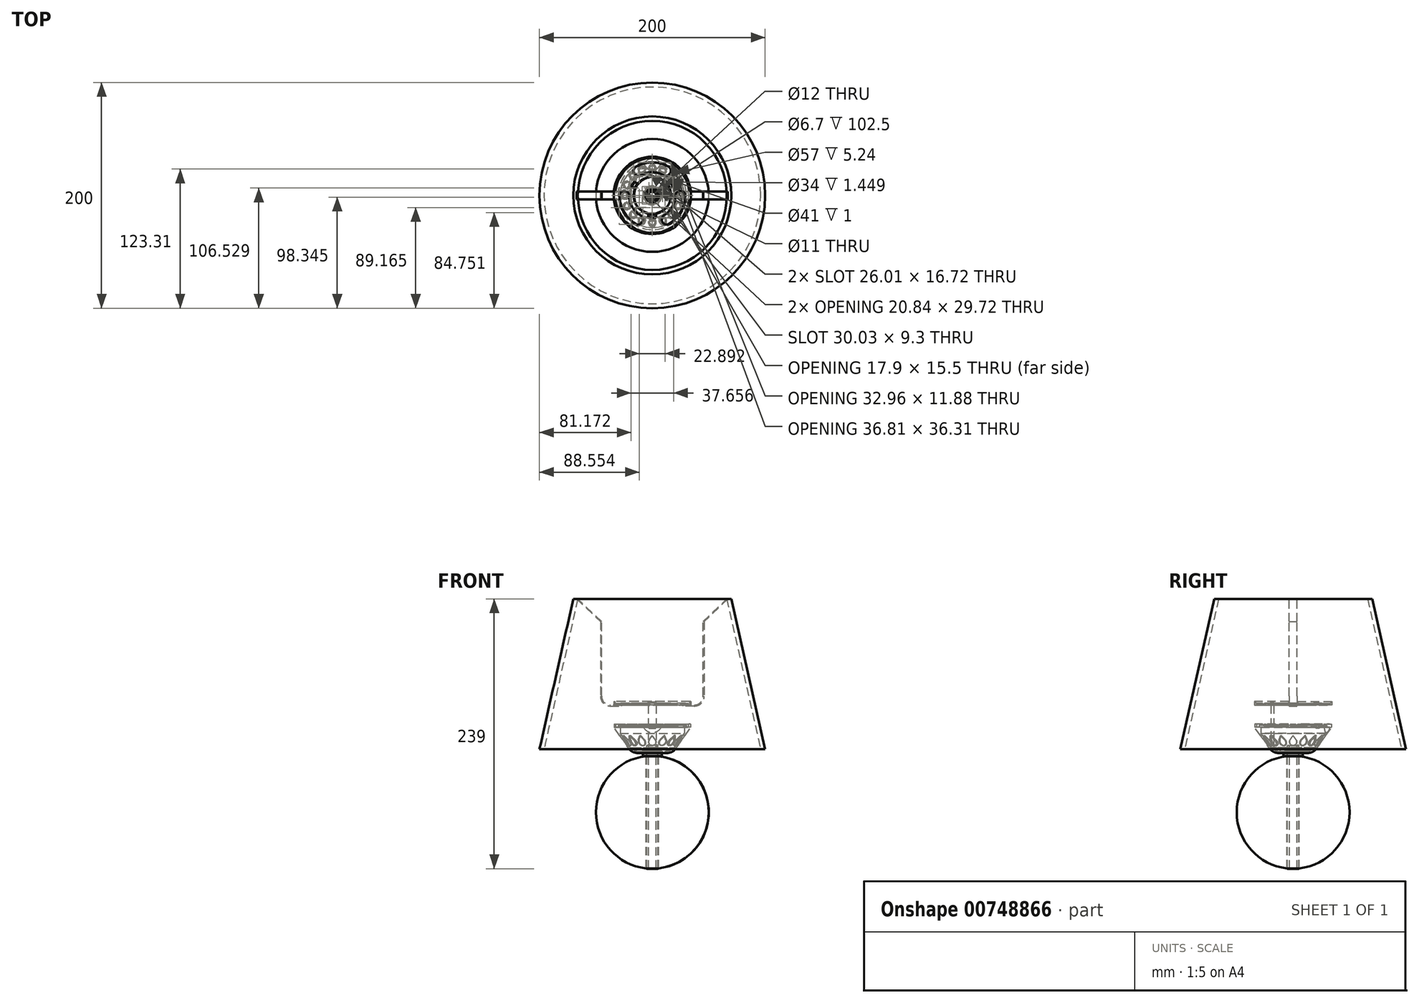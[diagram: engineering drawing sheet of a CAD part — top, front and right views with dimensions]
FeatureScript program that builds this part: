
annotation { "Feature Type Name" : "Feature", "Feature Type Description" : "" }
export const myFeature = defineFeature(function(context is Context, id is Id, definition is map)
    precondition{}
    {
        {
            assignVariable(context, id + "F0", {"name" : "e", "anyValue" : 1.5});
        }
        {
            var Q0;
            Q0=qCreatedBy(makeId("Front.planeOp"),FACE);
            var sketch = newSketch(context, id + "F1", { "sketchPlane" : qUnion([Q0])});
            skLineSegment(sketch, "E0", {"start": v(0, 0) * mm, "end": v(0, -12.75) * mm, "construction": true});
            skLineSegment(sketch, "E1.bottom", {"start": v(-3.35, 5) * mm, "end": v(-5, 5) * mm});
            skLineSegment(sketch, "E1.top", {"start": v(-3.35, -105) * mm, "end": v(-5, -105) * mm});
            skLineSegment(sketch, "E1.left", {"start": v(-3.35, 5) * mm, "end": v(-3.35, -105) * mm});
            skLineSegment(sketch, "E1.right", {"start": v(-5, 5) * mm, "end": v(-5, -105) * mm});
            skSolve(sketch);
        }
        {
            var Q0;
            Q0=makeQuery(id+"F1.imprint","IMPRINT",FACE,{"disambiguationData":[TD([[makeQuery(id+"F1.imprint","IMPRINT",EDGE,{"derivedFrom":sQuery(id+"F1.wireOp",EDGE,"E1.bottom")}),1.0]])]});
            var Q1;
            Q1=sQuery(id+"F1.wireOp",EDGE,"E0");
            revolve(context, id + "F2", {"surfaceOperationType" : NewSurfaceOperationType.NEW, "entities" : qUnion([Q0]), "axis" : qUnion([Q1]), "revolveType" : RevolveType.FULL});
        }
        {
            var Q0;
            Q0=qCreatedBy(makeId("Top.planeOp"),FACE);
            var sketch = newSketch(context, id + "F3", { "sketchPlane" : qUnion([Q0])});
            skLineSegment(sketch, "E2", {"start": v(0, 7) * mm, "end": v(-4.04, 7) * mm});
            skLineSegment(sketch, "E3", {"start": v(-4.04, 7) * mm, "end": v(-8.08, 0) * mm});
            skLineSegment(sketch, "E4", {"start": v(-8.08, 0) * mm, "end": v(0, 0) * mm, "construction": true});
            skLineSegment(sketch, "E5", {"start": v(0, 0) * mm, "end": v(0, 7) * mm, "construction": true});
            skLineSegment(sketch, "E6.MirrorCS", {"start": v(4.04, 7) * mm, "end": v(8.08, 0) * mm});
            skLineSegment(sketch, "E7.MirrorCS", {"start": v(0, 7) * mm, "end": v(4.04, 7) * mm});
            skLineSegment(sketch, "E8.MirrorCS", {"start": v(-4.04, -7) * mm, "end": v(-8.08, 0) * mm});
            skLineSegment(sketch, "E9.MirrorCS", {"start": v(0, -7) * mm, "end": v(-4.04, -7) * mm});
            skLineSegment(sketch, "E10.MirrorCS", {"start": v(0, -7) * mm, "end": v(4.04, -7) * mm});
            skLineSegment(sketch, "E11.MirrorCS", {"start": v(4.04, -7) * mm, "end": v(8.08, 0) * mm});
            skCircle(sketch, "E12", {"center": v(0, 0) * mm, "radius": 5 * mm});
            skSolve(sketch);
        }
        {
            var Q0;
            Q0=makeQuery(id+"F3.imprint","IMPRINT",FACE,{"disambiguationData":[TD([[makeQuery(id+"F3.imprint","IMPRINT",EDGE,{"derivedFrom":sQuery(id+"F3.wireOp",EDGE,"E2")}),1.0]])]});
            extrude(context, id + "F4", {"entities" : qUnion([Q0]), "oppositeDirection" : true, "depth" : 2.5 * mm, "offsetDistance" : 25 * mm});
        }
        {
            var Q0;
            Q0=makeQuery(id+"F4.opExtrude","CAP_FACE",FACE,{"disambiguationData":[OSD([sQuery(id+"F3.wireOp",EDGE,"E2"),sQuery(id+"F3.wireOp",EDGE,"E3"),sQuery(id+"F3.wireOp",EDGE,"E6.MirrorCS"),sQuery(id+"F3.wireOp",EDGE,"E7.MirrorCS"),sQuery(id+"F3.wireOp",EDGE,"E8.MirrorCS"),sQuery(id+"F3.wireOp",EDGE,"E9.MirrorCS"),sQuery(id+"F3.wireOp",EDGE,"E10.MirrorCS"),sQuery(id+"F3.wireOp",EDGE,"E11.MirrorCS"),sQuery(id+"F3.wireOp",EDGE,"E12")])],"isStart":false});
            var sketch = newSketch(context, id + "F5", { "sketchPlane" : qUnion([Q0])});
            skCircle(sketch, "E13", {"center": v(0, 0) * mm, "radius": 5 * mm});
            skCircle(sketch, "E14", {"center": v(0, 0) * mm, "radius": 8.5 * mm});
            skSolve(sketch);
        }
        {
            var Q0;
            Q0=makeQuery(id+"F5.imprint","IMPRINT",FACE,{"disambiguationData":[TD([[makeQuery(id+"F5.imprint","IMPRINT",EDGE,{"derivedFrom":sQuery(id+"F5.wireOp",EDGE,"E14")}),1.0]])]});
            var Q1;
            Q1=makeQuery(id+"F5.imprint","IMPRINT",FACE,{"disambiguationData":[TD([[makeQuery(id+"F5.imprint","IMPRINT",EDGE,{"derivedFrom":sQuery(id+"F5.wireOp",EDGE,"E13")}),1.0]])]});
            extrude(context, id + "F6", {"entities" : qUnion([Q0, Q1]), "depth" : 2.5 * mm, "offsetDistance" : 25 * mm});
        }
        {
            var Q0;
            Q0=qCreatedBy(makeId("Front.planeOp"),FACE);
            var sketch = newSketch(context, id + "F7", { "sketchPlane" : qUnion([Q0])});
            skArc(sketch, "E15", {"start": v(0, -5) * mm, "mid": v(-50, -55) * mm, "end": v(0, -105) * mm});
            skLineSegment(sketch, "E16.0", {"start": v(8.5, -5) * mm, "end": v(-8.5, -5) * mm});
            skLineSegment(sketch, "E17", {"start": v(0, -5) * mm, "end": v(0, -105) * mm});
            skSolve(sketch);
        }
        {
            var Q0;
            Q0=makeQuery(id+"F7.imprint","IMPRINT",FACE,{"disambiguationData":[TD([[makeQuery(id+"F7.imprint","IMPRINT",EDGE,{"derivedFrom":sQuery(id+"F7.wireOp",EDGE,"E15")}),1.0]])]});
            var Q1;
            Q1=sQuery(id+"F7.wireOp",EDGE,"E17");
            revolve(context, id + "F8", {"surfaceOperationType" : NewSurfaceOperationType.NEW, "entities" : qUnion([Q0]), "axis" : qUnion([Q1]), "revolveType" : RevolveType.FULL});
        }
        {
            var Q0;
            Q0=sQuery(id+"F3.wireOp",VERTEX,"E12.center");
            var Q1;
            Q1=makeQuery(id+"F8.opRevolve","SWEPT_BODY",BODY,{"disambiguationData":[OSD([sQuery(id+"F7.wireOp",EDGE,"E15"),sQuery(id+"F7.wireOp",EDGE,"E17")])]});
            hole(context, id + "F9", {"style" : HoleStyle.SIMPLE, "endStyle" : HoleEndStyle.THROUGH, "holeDiameter" : 11 * mm, "majorDiameter" : 5 * mm, "isTappedThrough" : true, "tappedDepth" : 12 * mm, "tapClearance" : 3, "locations" : qUnion([Q0]), "scope" : qUnion([Q1])});
        }
        {
            var Q0;
            Q0=qCreatedBy(makeId("Front.planeOp"),FACE);
            var sketch = newSketch(context, id + "F10", { "sketchPlane" : qUnion([Q0])});
            skLineSegment(sketch, "E18", {"start": v(0, -13.04) * mm, "end": v(0, 48.26) * mm, "construction": true});
            skLineSegment(sketch, "E19", {"start": v(-21.07, 1.76) * mm, "end": v(-34, 20.23) * mm});
            skLineSegment(sketch, "E20", {"start": v(-34, 20.23) * mm, "end": v(-34, 23.23) * mm});
            skLineSegment(sketch, "E21", {"start": v(-34, 23.23) * mm, "end": v(-32.5, 23.23) * mm});
            skLineSegment(sketch, "E22", {"start": v(-32.5, 23.23) * mm, "end": v(-32.5, 20.23) * mm});
            skLineSegment(sketch, "E23", {"start": v(-28.5, 15) * mm, "end": v(-19.5, 2.14) * mm});
            skLineSegment(sketch, "E24", {"start": v(-12.08, -1) * mm, "end": v(0, -1) * mm});
            skLineSegment(sketch, "E25", {"start": v(0, -1) * mm, "end": v(0, -2.5) * mm});
            skLineSegment(sketch, "E26.0", {"start": v(-8.08, -2.5) * mm, "end": v(-8.08, 0) * mm, "construction": true});
            skLineSegment(sketch, "E27.0", {"start": v(8.5, -2.5) * mm, "end": v(-8.5, -2.5) * mm});
            skLineSegment(sketch, "E28", {"start": v(-12.88, -2.5) * mm, "end": v(0, -2.5) * mm});
            skLineSegment(sketch, "E29", {"start": v(-28.5, 15) * mm, "end": v(-28.5, 20.23) * mm});
            skLineSegment(sketch, "E30", {"start": v(-28.5, 20.23) * mm, "end": v(-32.5, 20.23) * mm});
            skLineSegment(sketch, "E31", {"start": v(-17, 0.7) * mm, "end": v(-17, 2.14) * mm});
            skLineSegment(sketch, "E32", {"start": v(-17, 2.14) * mm, "end": v(-19.5, 2.14) * mm});
            skPoint(sketch, "E33.visualSharp", {"position": v(-18.08, -2.5) * mm});
            skArc(sketch, "E33.filletArc", {"start": v(-21.07, 1.76) * mm, "mid": v(-17.5, -1.37) * mm, "end": v(-12.88, -2.5) * mm});
            skPoint(sketch, "E34.visualSharp", {"position": v(-14.3, -1) * mm});
            skArc(sketch, "E34.filletArc", {"start": v(-17, 0.7) * mm, "mid": v(-14.68, -0.57) * mm, "end": v(-12.08, -1) * mm});
            skSolve(sketch);
        }
        {
            var Q0;
            {var subQ1=sQuery(id+"F10.wireOp",EDGE,"E19");Q0=makeQuery(id+"F10.imprint","IMPRINT",FACE,{"disambiguationData":[TD([[makeQuery(id+"F10.imprint","IMPRINT",EDGE,{"derivedFrom":subQ1}),-1.0]])]});}
            var Q1;
            Q1=sQuery(id+"F10.wireOp",EDGE,"E18");
            revolve(context, id + "F11", {"surfaceOperationType" : NewSurfaceOperationType.NEW, "entities" : qUnion([Q0]), "axis" : qUnion([Q1]), "revolveType" : RevolveType.FULL});
        }
        {
            var Q0;
            Q0=makeQuery(id+"F11.opRevolve","SWEPT_FACE",FACE,{"disambiguationData":[OSD([sQuery(id+"F10.wireOp",EDGE,"E24")])]});
            var sketch = newSketch(context, id + "F12", { "sketchPlane" : qUnion([Q0])});
            skLineSegment(sketch, "E35", {"start": v(-4.04, -7) * mm, "end": v(-8.08, 0) * mm, "construction": true});
            skLineSegment(sketch, "E36", {"start": v(4.04, -7) * mm, "end": v(-4.04, -7) * mm, "construction": true});
            skLineSegment(sketch, "E37", {"start": v(4.04, -7) * mm, "end": v(8.08, 0) * mm, "construction": true});
            skLineSegment(sketch, "E38", {"start": v(4.04, 7) * mm, "end": v(8.08, 0) * mm, "construction": true});
            skLineSegment(sketch, "E39", {"start": v(-4.04, 7) * mm, "end": v(4.04, 7) * mm, "construction": true});
            skLineSegment(sketch, "E40", {"start": v(-4.04, 7) * mm, "end": v(-8.08, 0) * mm, "construction": true});
            skLineSegment(sketch, "E41.0", {"start": v(-4.47, 7.75) * mm, "end": v(4.47, 7.75) * mm});
            skLineSegment(sketch, "E41.1", {"start": v(-4.47, -7.75) * mm, "end": v(-8.95, 0) * mm});
            skLineSegment(sketch, "E41.2", {"start": v(4.47, -7.75) * mm, "end": v(-4.47, -7.75) * mm});
            skLineSegment(sketch, "E41.3", {"start": v(-4.47, 7.75) * mm, "end": v(-8.95, 0) * mm});
            skLineSegment(sketch, "E41.4", {"start": v(4.47, -7.75) * mm, "end": v(8.95, 0) * mm});
            skLineSegment(sketch, "E41.5", {"start": v(4.47, 7.75) * mm, "end": v(8.95, 0) * mm});
            skSolve(sketch);
        }
        {
            var Q0;
            Q0=makeQuery(id+"F12.imprint","IMPRINT",FACE,{"disambiguationData":[TD([[makeQuery(id+"F12.imprint","IMPRINT",EDGE,{"derivedFrom":sQuery(id+"F12.wireOp",EDGE,"E41.0")}),-1.0]])]});
            extrude(context, id + "F13", {"entities" : qUnion([Q0]), "operationType" : NewBodyOperationType.REMOVE, "endBound" : BoundingType.UP_TO_NEXT, "oppositeDirection" : true, "depth" : 25 * mm, "offsetDistance" : 25 * mm});
        }
        {
            var Q0;
            Q0=makeQuery(id+"F11.opRevolve","SWEPT_FACE",FACE,{"disambiguationData":[OSD([sQuery(id+"F10.wireOp",EDGE,"E30")])]});
            var sketch = newSketch(context, id + "F14", { "sketchPlane" : qUnion([Q0])});
            skCircle(sketch, "E42", {"center": v(0, 0) * mm, "radius": 30.3 * mm});
            skLineSegment(sketch, "E43", {"start": v(0, 0) * mm, "end": v(-3.08, 15.85) * mm, "construction": true});
            skLineSegment(sketch, "E44.MirrorCS", {"start": v(0, 0) * mm, "end": v(3.08, 15.85) * mm, "construction": true});
            skLineSegment(sketch, "E45.1.0", {"start": v(0, 0) * mm, "end": v(-12.19, -10.6) * mm, "construction": true});
            skLineSegment(sketch, "E45.1.1", {"start": v(0, 0) * mm, "end": v(-15.27, -5.26) * mm, "construction": true});
            skLineSegment(sketch, "E45.2.0", {"start": v(0, 0) * mm, "end": v(15.27, -5.26) * mm, "construction": true});
            skLineSegment(sketch, "E45.2.1", {"start": v(0, 0) * mm, "end": v(12.19, -10.6) * mm, "construction": true});
            skLineSegment(sketch, "E46", {"start": v(-3.08, 15.85) * mm, "end": v(-3.8, 19.53) * mm});
            skLineSegment(sketch, "E47", {"start": v(3.08, 15.85) * mm, "end": v(3.8, 19.53) * mm});
            skArc(sketch, "E48", {"start": v(3.8, 19.53) * mm, "mid": v(0, 19.9) * mm, "end": v(-3.8, 19.53) * mm, "construction": true});
            skArc(sketch, "E49", {"start": v(-3.8, 19.53) * mm, "mid": v(-17.23, 9.95) * mm, "end": v(-18.82, -6.48) * mm});
            skArc(sketch, "E50", {"start": v(-3.08, 15.85) * mm, "mid": v(-13.99, 8.07) * mm, "end": v(-15.27, -5.26) * mm});
            skArc(sketch, "E51", {"start": v(3.08, 15.85) * mm, "mid": v(0, 16.15) * mm, "end": v(-3.08, 15.85) * mm, "construction": true});
            skArc(sketch, "E52", {"start": v(15.27, -5.26) * mm, "mid": v(13.99, 8.07) * mm, "end": v(3.08, 15.85) * mm});
            skLineSegment(sketch, "E53", {"start": v(15.27, -5.26) * mm, "end": v(18.82, -6.48) * mm});
            skArc(sketch, "E54", {"start": v(18.82, -6.48) * mm, "mid": v(17.23, 9.95) * mm, "end": v(3.8, 19.53) * mm});
            skArc(sketch, "E55", {"start": v(15.02, -13.06) * mm, "mid": v(17.23, -9.95) * mm, "end": v(18.82, -6.48) * mm, "construction": true});
            skLineSegment(sketch, "E56", {"start": v(12.19, -10.6) * mm, "end": v(15.02, -13.06) * mm});
            skArc(sketch, "E57", {"start": v(12.19, -10.6) * mm, "mid": v(13.99, -8.08) * mm, "end": v(15.27, -5.26) * mm, "construction": true});
            skArc(sketch, "E58", {"start": v(-12.19, -10.6) * mm, "mid": v(0, -16.15) * mm, "end": v(12.19, -10.6) * mm});
            skLineSegment(sketch, "E59", {"start": v(-12.19, -10.6) * mm, "end": v(-15.02, -13.06) * mm});
            skArc(sketch, "E60", {"start": v(-15.27, -5.26) * mm, "mid": v(-13.99, -8.07) * mm, "end": v(-12.19, -10.6) * mm, "construction": true});
            skLineSegment(sketch, "E61", {"start": v(-15.27, -5.26) * mm, "end": v(-18.82, -6.48) * mm});
            skArc(sketch, "E62", {"start": v(-18.82, -6.48) * mm, "mid": v(-17.23, -9.95) * mm, "end": v(-15.02, -13.06) * mm, "construction": true});
            skArc(sketch, "E63", {"start": v(-15.02, -13.06) * mm, "mid": v(0, -19.9) * mm, "end": v(15.02, -13.06) * mm});
            skSolve(sketch);
        }
        {
            var Q0;
            Q0=makeQuery(id+"F14.imprint","IMPRINT",FACE,{"disambiguationData":[TD([[makeQuery(id+"F14.imprint","IMPRINT",EDGE,{"derivedFrom":sQuery(id+"F14.wireOp",EDGE,"E46")}),-1.0]])]});
            var Q1;
            Q1=makeQuery(id+"F14.imprint","IMPRINT",FACE,{"disambiguationData":[TD([[makeQuery(id+"F14.imprint","IMPRINT",EDGE,{"derivedFrom":sQuery(id+"F14.wireOp",EDGE,"E42")}),1.0]])]});
            extrude(context, id + "F15", {"entities" : qUnion([Q0, Q1]), "depth" : 1.5 * mm, "offsetDistance" : 25 * mm});
        }
        {
            var Q0;
            Q0=makeQuery(id+"F15.opExtrude","CAP_FACE",FACE,{"disambiguationData":[OSD([sQuery(id+"F10.wireOp",EDGE,"E29"),sQuery(id+"F10.wireOp",EDGE,"E30"),sQuery(id+"F14.wireOp",EDGE,"E46"),sQuery(id+"F14.wireOp",EDGE,"E47"),sQuery(id+"F14.wireOp",EDGE,"E49"),sQuery(id+"F14.wireOp",EDGE,"E50"),sQuery(id+"F14.wireOp",EDGE,"E52"),sQuery(id+"F14.wireOp",EDGE,"E53"),sQuery(id+"F14.wireOp",EDGE,"E54"),sQuery(id+"F14.wireOp",EDGE,"E56"),sQuery(id+"F14.wireOp",EDGE,"E58"),sQuery(id+"F14.wireOp",EDGE,"E59"),sQuery(id+"F14.wireOp",EDGE,"E61"),sQuery(id+"F14.wireOp",EDGE,"E63")])],"isStart":false});
            var sketch = newSketch(context, id + "F16", { "sketchPlane" : qUnion([Q0])});
            skLineSegment(sketch, "E64.bottom", {"start": v(2.5, 26.95) * mm, "end": v(-2.5, 26.95) * mm});
            skLineSegment(sketch, "E64.top", {"start": v(2.5, 21.95) * mm, "end": v(-2.5, 21.95) * mm});
            skLineSegment(sketch, "E64.left", {"start": v(2.5, 26.95) * mm, "end": v(2.5, 21.95) * mm});
            skLineSegment(sketch, "E64.right", {"start": v(-2.5, 26.95) * mm, "end": v(-2.5, 21.95) * mm});
            skPoint(sketch, "E64.middle", {"position": v(0, 24.45) * mm});
            skLineSegment(sketch, "E65.1.0", {"start": v(-8, 25.86) * mm, "end": v(-12.62, 23.94) * mm});
            skLineSegment(sketch, "E65.1.1", {"start": v(-12.62, 23.94) * mm, "end": v(-10.7, 19.32) * mm});
            skLineSegment(sketch, "E65.1.2", {"start": v(-6.1, 21.24) * mm, "end": v(-10.7, 19.32) * mm});
            skLineSegment(sketch, "E65.1.3", {"start": v(-8, 25.86) * mm, "end": v(-6.1, 21.24) * mm});
            skLineSegment(sketch, "E65.2.0", {"start": v(-17.29, 20.82) * mm, "end": v(-20.82, 17.29) * mm});
            skLineSegment(sketch, "E65.2.1", {"start": v(-20.82, 17.29) * mm, "end": v(-17.29, 13.75) * mm});
            skLineSegment(sketch, "E65.2.2", {"start": v(-13.75, 17.29) * mm, "end": v(-17.29, 13.75) * mm});
            skLineSegment(sketch, "E65.2.3", {"start": v(-17.29, 20.82) * mm, "end": v(-13.75, 17.29) * mm});
            skLineSegment(sketch, "E65.3.0", {"start": v(-23.94, 12.62) * mm, "end": v(-25.86, 8) * mm});
            skLineSegment(sketch, "E65.3.1", {"start": v(-25.86, 8) * mm, "end": v(-21.24, 6.1) * mm});
            skLineSegment(sketch, "E65.3.2", {"start": v(-19.32, 10.7) * mm, "end": v(-21.24, 6.1) * mm});
            skLineSegment(sketch, "E65.3.3", {"start": v(-23.94, 12.62) * mm, "end": v(-19.32, 10.7) * mm});
            skLineSegment(sketch, "E65.4.0", {"start": v(-26.95, 2.5) * mm, "end": v(-26.95, -2.5) * mm});
            skLineSegment(sketch, "E65.4.1", {"start": v(-26.95, -2.5) * mm, "end": v(-21.95, -2.5) * mm});
            skLineSegment(sketch, "E65.4.2", {"start": v(-21.95, 2.5) * mm, "end": v(-21.95, -2.5) * mm});
            skLineSegment(sketch, "E65.4.3", {"start": v(-26.95, 2.5) * mm, "end": v(-21.95, 2.5) * mm});
            skLineSegment(sketch, "E65.5.0", {"start": v(-25.86, -8) * mm, "end": v(-23.94, -12.62) * mm});
            skLineSegment(sketch, "E65.5.1", {"start": v(-23.94, -12.62) * mm, "end": v(-19.32, -10.7) * mm});
            skLineSegment(sketch, "E65.5.2", {"start": v(-21.24, -6.1) * mm, "end": v(-19.32, -10.7) * mm});
            skLineSegment(sketch, "E65.5.3", {"start": v(-25.86, -8) * mm, "end": v(-21.24, -6.1) * mm});
            skLineSegment(sketch, "E65.6.0", {"start": v(-20.82, -17.29) * mm, "end": v(-17.29, -20.82) * mm});
            skLineSegment(sketch, "E65.6.1", {"start": v(-17.29, -20.82) * mm, "end": v(-13.75, -17.29) * mm});
            skLineSegment(sketch, "E65.6.2", {"start": v(-17.29, -13.75) * mm, "end": v(-13.75, -17.29) * mm});
            skLineSegment(sketch, "E65.6.3", {"start": v(-20.82, -17.29) * mm, "end": v(-17.29, -13.75) * mm});
            skLineSegment(sketch, "E65.7.0", {"start": v(-12.62, -23.94) * mm, "end": v(-8, -25.86) * mm});
            skLineSegment(sketch, "E65.7.1", {"start": v(-8, -25.86) * mm, "end": v(-6.1, -21.24) * mm});
            skLineSegment(sketch, "E65.7.2", {"start": v(-10.7, -19.32) * mm, "end": v(-6.1, -21.24) * mm});
            skLineSegment(sketch, "E65.7.3", {"start": v(-12.62, -23.94) * mm, "end": v(-10.7, -19.32) * mm});
            skLineSegment(sketch, "E65.8.0", {"start": v(-2.5, -26.95) * mm, "end": v(2.5, -26.95) * mm});
            skLineSegment(sketch, "E65.8.1", {"start": v(2.5, -26.95) * mm, "end": v(2.5, -21.95) * mm});
            skLineSegment(sketch, "E65.8.2", {"start": v(-2.5, -21.95) * mm, "end": v(2.5, -21.95) * mm});
            skLineSegment(sketch, "E65.8.3", {"start": v(-2.5, -26.95) * mm, "end": v(-2.5, -21.95) * mm});
            skLineSegment(sketch, "E65.9.0", {"start": v(8, -25.86) * mm, "end": v(12.62, -23.94) * mm});
            skLineSegment(sketch, "E65.9.1", {"start": v(12.62, -23.94) * mm, "end": v(10.7, -19.32) * mm});
            skLineSegment(sketch, "E65.9.2", {"start": v(6.1, -21.24) * mm, "end": v(10.7, -19.32) * mm});
            skLineSegment(sketch, "E65.9.3", {"start": v(8, -25.86) * mm, "end": v(6.1, -21.24) * mm});
            skLineSegment(sketch, "E65.10.0", {"start": v(17.29, -20.82) * mm, "end": v(20.82, -17.29) * mm});
            skLineSegment(sketch, "E65.10.1", {"start": v(20.82, -17.29) * mm, "end": v(17.29, -13.75) * mm});
            skLineSegment(sketch, "E65.10.2", {"start": v(13.75, -17.29) * mm, "end": v(17.29, -13.75) * mm});
            skLineSegment(sketch, "E65.10.3", {"start": v(17.29, -20.82) * mm, "end": v(13.75, -17.29) * mm});
            skLineSegment(sketch, "E65.11.0", {"start": v(23.94, -12.62) * mm, "end": v(25.86, -8) * mm});
            skLineSegment(sketch, "E65.11.1", {"start": v(25.86, -8) * mm, "end": v(21.24, -6.1) * mm});
            skLineSegment(sketch, "E65.11.2", {"start": v(19.32, -10.7) * mm, "end": v(21.24, -6.1) * mm});
            skLineSegment(sketch, "E65.11.3", {"start": v(23.94, -12.62) * mm, "end": v(19.32, -10.7) * mm});
            skLineSegment(sketch, "E65.12.0", {"start": v(26.95, -2.5) * mm, "end": v(26.95, 2.5) * mm});
            skLineSegment(sketch, "E65.12.1", {"start": v(26.95, 2.5) * mm, "end": v(21.95, 2.5) * mm});
            skLineSegment(sketch, "E65.12.2", {"start": v(21.95, -2.5) * mm, "end": v(21.95, 2.5) * mm});
            skLineSegment(sketch, "E65.12.3", {"start": v(26.95, -2.5) * mm, "end": v(21.95, -2.5) * mm});
            skLineSegment(sketch, "E65.13.0", {"start": v(25.86, 8) * mm, "end": v(23.94, 12.62) * mm});
            skLineSegment(sketch, "E65.13.1", {"start": v(23.94, 12.62) * mm, "end": v(19.32, 10.7) * mm});
            skLineSegment(sketch, "E65.13.2", {"start": v(21.24, 6.1) * mm, "end": v(19.32, 10.7) * mm});
            skLineSegment(sketch, "E65.13.3", {"start": v(25.86, 8) * mm, "end": v(21.24, 6.1) * mm});
            skLineSegment(sketch, "E65.14.0", {"start": v(20.82, 17.29) * mm, "end": v(17.29, 20.82) * mm});
            skLineSegment(sketch, "E65.14.1", {"start": v(17.29, 20.82) * mm, "end": v(13.75, 17.29) * mm});
            skLineSegment(sketch, "E65.14.2", {"start": v(17.29, 13.75) * mm, "end": v(13.75, 17.29) * mm});
            skLineSegment(sketch, "E65.14.3", {"start": v(20.82, 17.29) * mm, "end": v(17.29, 13.75) * mm});
            skLineSegment(sketch, "E65.15.0", {"start": v(12.62, 23.94) * mm, "end": v(8, 25.86) * mm});
            skLineSegment(sketch, "E65.15.1", {"start": v(8, 25.86) * mm, "end": v(6.1, 21.24) * mm});
            skLineSegment(sketch, "E65.15.2", {"start": v(10.7, 19.32) * mm, "end": v(6.1, 21.24) * mm});
            skLineSegment(sketch, "E65.15.3", {"start": v(12.62, 23.94) * mm, "end": v(10.7, 19.32) * mm});
            skPoint(sketch, "E65.center", {"position": v(0, 0) * mm});
            skSolve(sketch);
        }
        {
            var Q0;
            Q0 = qSketchRegion(id + "F16", true);
            extrude(context, id + "F17", {"entities" : qUnion([Q0]), "operationType" : NewBodyOperationType.ADD, "depth" : 1 * mm, "offsetDistance" : 25 * mm});
        }
        {
            var Q0;
            Q0=makeQuery(id+"F15.opExtrude","CAP_FACE",FACE,{"disambiguationData":[OSD([sQuery(id+"F10.wireOp",EDGE,"E29"),sQuery(id+"F10.wireOp",EDGE,"E30"),sQuery(id+"F14.wireOp",EDGE,"E46"),sQuery(id+"F14.wireOp",EDGE,"E47"),sQuery(id+"F14.wireOp",EDGE,"E49"),sQuery(id+"F14.wireOp",EDGE,"E50"),sQuery(id+"F14.wireOp",EDGE,"E52"),sQuery(id+"F14.wireOp",EDGE,"E53"),sQuery(id+"F14.wireOp",EDGE,"E54"),sQuery(id+"F14.wireOp",EDGE,"E56"),sQuery(id+"F14.wireOp",EDGE,"E58"),sQuery(id+"F14.wireOp",EDGE,"E59"),sQuery(id+"F14.wireOp",EDGE,"E61"),sQuery(id+"F14.wireOp",EDGE,"E63")])],"isStart":true});
            var sketch = newSketch(context, id + "F18", { "sketchPlane" : qUnion([Q0])});
            skLineSegment(sketch, "E66.bottom", {"start": v(3, -28.3) * mm, "end": v(-3, -28.3) * mm});
            skLineSegment(sketch, "E66.top", {"start": v(3, -20.3) * mm, "end": v(-3, -20.3) * mm});
            skLineSegment(sketch, "E66.left", {"start": v(3, -28.3) * mm, "end": v(3, -20.3) * mm});
            skLineSegment(sketch, "E66.right", {"start": v(-3, -28.3) * mm, "end": v(-3, -20.3) * mm});
            skPoint(sketch, "E66.middle", {"position": v(0, -24.3) * mm});
            skSolve(sketch);
        }
        {
            var Q0;
            Q0 = qSketchRegion(id + "F18", true);
            extrude(context, id + "F19", {"entities" : qUnion([Q0]), "operationType" : NewBodyOperationType.ADD, "depth" : 1 * mm, "offsetDistance" : 25 * mm});
        }
        {
            var Q0;
            Q0=makeQuery(id+"F11.opRevolve","SWEPT_FACE",FACE,{"disambiguationData":[OSD([sQuery(id+"F10.wireOp",EDGE,"E30")])]});
            var sketch = newSketch(context, id + "F20", { "sketchPlane" : qUnion([Q0])});
            skArc(sketch, "E67", {"start": v(0, 32.5) * mm, "mid": v(-4.5, 31.13) * mm, "end": v(-7.5, 27.5) * mm});
            skLineSegment(sketch, "E68", {"start": v(-7.5, 27.5) * mm, "end": v(0, 27.5) * mm});
            skArc(sketch, "E69.MirrorCS", {"start": v(0, 32.5) * mm, "mid": v(4.5, 31.13) * mm, "end": v(7.5, 27.5) * mm});
            skLineSegment(sketch, "E70.MirrorCS", {"start": v(7.5, 27.5) * mm, "end": v(0, 27.5) * mm});
            skSolve(sketch);
        }
        {
            var Q0;
            Q0 = qSketchRegion(id + "F20", true);
            var Q1;
            Q1=sQuery(id+"F20.wireOp",EDGE,"E68");
            revolve(context, id + "F21", {"operationType" : NewBodyOperationType.REMOVE, "surfaceOperationType" : NewSurfaceOperationType.NEW, "entities" : qUnion([Q0]), "axis" : qUnion([Q1]), "revolveType" : RevolveType.FULL});
        }
        {
            var Q0;
            Q0=makeQuery(id+"F11.opRevolve","SWEPT_FACE",FACE,{"disambiguationData":[OSD([sQuery(id+"F10.wireOp",EDGE,"E21")])]});
            var sketch = newSketch(context, id + "F22", { "sketchPlane" : qUnion([Q0])});
            skLineSegment(sketch, "E71", {"start": v(-34, 0) * mm, "end": v(-34, 4) * mm});
            skLineSegment(sketch, "E72", {"start": v(-34, 4) * mm, "end": v(-32.25, 4) * mm});
            skLineSegment(sketch, "E73", {"start": v(-32.25, 4) * mm, "end": v(-32.25, 0) * mm});
            skLineSegment(sketch, "E74.MirrorCS", {"start": v(-34, -4) * mm, "end": v(-32.25, -4) * mm});
            skLineSegment(sketch, "E75.MirrorCS", {"start": v(-34, 0) * mm, "end": v(-34, -4) * mm});
            skLineSegment(sketch, "E76.MirrorCS", {"start": v(-32.25, -4) * mm, "end": v(-32.25, 0) * mm});
            skLineSegment(sketch, "E77.MirrorCS", {"start": v(34, 0) * mm, "end": v(34, 4) * mm});
            skLineSegment(sketch, "E78.MirrorCS", {"start": v(34, 4) * mm, "end": v(32.25, 4) * mm});
            skLineSegment(sketch, "E79.MirrorCS", {"start": v(32.25, 4) * mm, "end": v(32.25, 0) * mm});
            skLineSegment(sketch, "E80.MirrorCS", {"start": v(32.25, -4) * mm, "end": v(32.25, 0) * mm});
            skLineSegment(sketch, "E81.MirrorCS", {"start": v(34, 0) * mm, "end": v(34, -4) * mm});
            skLineSegment(sketch, "E82.MirrorCS", {"start": v(34, -4) * mm, "end": v(32.25, -4) * mm});
            skSolve(sketch);
        }
        {
            var Q0;
            Q0 = qSketchRegion(id + "F22", true);
            var Q1;
            Q1=makeQuery(id+"F11.opRevolve","SWEPT_FACE",FACE,{"disambiguationData":[OSD([sQuery(id+"F10.wireOp",EDGE,"E30")])]});
            extrude(context, id + "F23", {"entities" : qUnion([Q0]), "operationType" : NewBodyOperationType.REMOVE, "endBound" : BoundingType.UP_TO_SURFACE, "oppositeDirection" : true, "depth" : 25 * mm, "endBoundEntityFace" : qUnion([Q1]), "offsetDistance" : 25 * mm});
        }
        {
            var Q0;
            Q0=sQuery(id+"F14.wireOp",VERTEX,"E42.center");
            var Q1;
            Q1=makeQuery(id+"F15.opExtrude","SWEPT_BODY",BODY,{"disambiguationData":[OSD([sQuery(id+"F14.wireOp",EDGE,"E42"),sQuery(id+"F14.wireOp",EDGE,"E46"),sQuery(id+"F14.wireOp",EDGE,"E47"),sQuery(id+"F14.wireOp",EDGE,"E49"),sQuery(id+"F14.wireOp",EDGE,"E50"),sQuery(id+"F14.wireOp",EDGE,"E52"),sQuery(id+"F14.wireOp",EDGE,"E53"),sQuery(id+"F14.wireOp",EDGE,"E54"),sQuery(id+"F14.wireOp",EDGE,"E56"),sQuery(id+"F14.wireOp",EDGE,"E58"),sQuery(id+"F14.wireOp",EDGE,"E59"),sQuery(id+"F14.wireOp",EDGE,"E61"),sQuery(id+"F14.wireOp",EDGE,"E63")])]});
            hole(context, id + "F24", {"style" : HoleStyle.SIMPLE, "endStyle" : HoleEndStyle.THROUGH, "oppositeDirection" : true, "holeDiameter" : 12 * mm, "majorDiameter" : 5 * mm, "isTappedThrough" : true, "tappedDepth" : 12 * mm, "tapClearance" : 3, "locations" : qUnion([Q0]), "scope" : qUnion([Q1])});
        }
        {
            var Q0;
            Q0=qCreatedBy(makeId("Top.planeOp"),FACE);
            cPlane(context, id + "F25", {"entities" : qUnion([Q0]), "cplaneType" : CPlaneType.OFFSET, "offset" : 40 * mm, "width" : 150 * mm, "height" : 150 * mm});
        }
        {
            var Q0;
            Q0=qCreatedBy(makeId("Front.planeOp"),FACE);
            var sketch = newSketch(context, id + "F26", { "sketchPlane" : qUnion([Q0])});
            skLineSegment(sketch, "E83", {"start": v(-70, 134) * mm, "end": v(-100, 1) * mm});
            skLineSegment(sketch, "E84", {"start": v(-100, 1) * mm, "end": v(-96, 1) * mm});
            skLineSegment(sketch, "E85", {"start": v(-96, 1) * mm, "end": v(-66, 134) * mm});
            skLineSegment(sketch, "E86", {"start": v(-66, 134) * mm, "end": v(-70, 134) * mm});
            skLineSegment(sketch, "E87", {"start": v(0, 0) * mm, "end": v(0, 118.67) * mm, "construction": true});
            skLineSegment(sketch, "E88", {"start": v(-32.12, 40) * mm, "end": v(45.05, 40) * mm, "construction": true});
            skSolve(sketch);
        }
        {
            var Q0;
            Q0=makeQuery(id+"F26.imprint","IMPRINT",FACE,{"disambiguationData":[TD([[makeQuery(id+"F26.imprint","IMPRINT",EDGE,{"derivedFrom":sQuery(id+"F26.wireOp",EDGE,"E83")}),1.0]])]});
            var Q1;
            Q1=sQuery(id+"F26.wireOp",EDGE,"E87");
            revolve(context, id + "F27", {"surfaceOperationType" : NewSurfaceOperationType.NEW, "entities" : qUnion([Q0]), "axis" : qUnion([Q1]), "revolveType" : RevolveType.FULL});
        }
        {
            var Q0;
            Q0=qCreatedBy(id+"F25.planeOp",FACE);
            var sketch = newSketch(context, id + "F28", { "sketchPlane" : qUnion([Q0])});
            skCircle(sketch, "E89", {"center": v(0, 0) * mm, "radius": 20.5 * mm});
            skCircle(sketch, "E90", {"center": v(0, 0) * mm, "radius": 32.25 * mm});
            skSolve(sketch);
        }
        {
            var Q0;
            Q0=makeQuery(id+"F28.imprint","IMPRINT",FACE,{"disambiguationData":[TD([[makeQuery(id+"F28.imprint","IMPRINT",EDGE,{"derivedFrom":sQuery(id+"F28.wireOp",EDGE,"E89")}),-1.0]])]});
            extrude(context, id + "F29", {"entities" : qUnion([Q0]), "depth" : 1 * mm, "offsetDistance" : 25 * mm});
        }
        {
            var Q0;
            Q0=qCreatedBy(makeId("Front.planeOp"),FACE);
            var sketch = newSketch(context, id + "F30", { "sketchPlane" : qUnion([Q0])});
            skLineSegment(sketch, "E91", {"start": v(96, 1) * mm, "end": v(66, 134) * mm, "construction": true});
            skLineSegment(sketch, "E92", {"start": v(-66, 134) * mm, "end": v(-96, 1) * mm, "construction": true});
            skLineSegment(sketch, "E93", {"start": v(-20.5, 41) * mm, "end": v(-32.25, 41) * mm, "construction": true});
            skLineSegment(sketch, "E94", {"start": v(32.25, 41) * mm, "end": v(20.5, 41) * mm, "construction": true});
            skLineSegment(sketch, "E95", {"start": v(-67, 134) * mm, "end": v(-46, 114) * mm});
            skLineSegment(sketch, "E96", {"start": v(-46, 114) * mm, "end": v(-46, 48) * mm});
            skLineSegment(sketch, "E97", {"start": v(-37, 39) * mm, "end": v(-27.25, 39) * mm});
            skLineSegment(sketch, "E98", {"start": v(-27.25, 39) * mm, "end": v(-27.25, 40) * mm});
            skLineSegment(sketch, "E99", {"start": v(-27.25, 40) * mm, "end": v(-37, 40) * mm});
            skLineSegment(sketch, "E100", {"start": v(-45, 48) * mm, "end": v(-45, 114) * mm});
            skLineSegment(sketch, "E101", {"start": v(-45, 114) * mm, "end": v(-66, 134) * mm});
            skLineSegment(sketch, "E102", {"start": v(-66, 134) * mm, "end": v(-67, 134) * mm});
            skLineSegment(sketch, "E103", {"start": v(-20.5, 40) * mm, "end": v(-32.25, 40) * mm, "construction": true});
            skLineSegment(sketch, "E104", {"start": v(32.25, 40) * mm, "end": v(20.5, 40) * mm, "construction": true});
            skPoint(sketch, "E105.visualSharp", {"position": v(-45, 40) * mm});
            skArc(sketch, "E105.filletArc", {"start": v(-45, 48) * mm, "mid": v(-42.66, 42.34) * mm, "end": v(-37, 40) * mm});
            skPoint(sketch, "E106.visualSharp", {"position": v(-46, 39) * mm});
            skArc(sketch, "E106.filletArc", {"start": v(-46, 48) * mm, "mid": v(-43.36, 41.64) * mm, "end": v(-37, 39) * mm});
            skLineSegment(sketch, "E107", {"start": v(66, 134) * mm, "end": v(70, 134) * mm, "construction": true});
            skLineSegment(sketch, "E108", {"start": v(-70, 134) * mm, "end": v(-66, 134) * mm, "construction": true});
            skLineSegment(sketch, "E109.MirrorCS", {"start": v(67, 134) * mm, "end": v(46, 114) * mm});
            skLineSegment(sketch, "E110.MirrorCS", {"start": v(45, 114) * mm, "end": v(66, 134) * mm});
            skLineSegment(sketch, "E111.MirrorCS", {"start": v(66, 134) * mm, "end": v(67, 134) * mm});
            skLineSegment(sketch, "E112.MirrorCS", {"start": v(46, 114) * mm, "end": v(46, 48) * mm});
            skLineSegment(sketch, "E113.MirrorCS", {"start": v(45, 48) * mm, "end": v(45, 114) * mm});
            skArc(sketch, "E114.MirrorCS", {"start": v(46, 48) * mm, "mid": v(43.36, 41.64) * mm, "end": v(37, 39) * mm});
            skArc(sketch, "E115.MirrorCS", {"start": v(45, 48) * mm, "mid": v(42.66, 42.34) * mm, "end": v(37, 40) * mm});
            skLineSegment(sketch, "E116.MirrorCS", {"start": v(37, 39) * mm, "end": v(27.25, 39) * mm});
            skLineSegment(sketch, "E117.MirrorCS", {"start": v(27.25, 40) * mm, "end": v(37, 40) * mm});
            skLineSegment(sketch, "E118.MirrorCS", {"start": v(27.25, 39) * mm, "end": v(27.25, 40) * mm});
            skSolve(sketch);
        }
        {
            var Q0;
            Q0=makeQuery(id+"F30.imprint","IMPRINT",FACE,{"disambiguationData":[TD([[makeQuery(id+"F30.imprint","IMPRINT",EDGE,{"derivedFrom":sQuery(id+"F30.wireOp",EDGE,"E95")}),1.0]])]});
            var Q1;
            Q1=makeQuery(id+"F30.imprint","IMPRINT",FACE,{"disambiguationData":[TD([[makeQuery(id+"F30.imprint","IMPRINT",EDGE,{"derivedFrom":sQuery(id+"F30.wireOp",EDGE,"E109.MirrorCS")}),-1.0]])]});
            extrude(context, id + "F31", {"entities" : qUnion([Q0, Q1]), "endBound" : BoundingType.SYMMETRIC, "depth" : 7 * mm, "offsetDistance" : 25 * mm});
        }
        {
            var Q0;
            Q0=qCreatedBy(id+"F25.planeOp",FACE);
            var sketch = newSketch(context, id + "F32", { "sketchPlane" : qUnion([Q0])});
            skCircle(sketch, "E119", {"center": v(0, 0) * mm, "radius": 34.25 * mm});
            skArc(sketch, "E120", {"start": v(2.5, -16.3) * mm, "mid": v(14.29, -8.25) * mm, "end": v(15.37, 5.99) * mm});
            skCircle(sketch, "E121", {"center": v(0, 0) * mm, "radius": 33.25 * mm});
            skLineSegment(sketch, "E122", {"start": v(-2.5, -16.3) * mm, "end": v(-2.5, -19.8) * mm});
            skLineSegment(sketch, "E123", {"start": v(-2.5, -19.8) * mm, "end": v(0, -19.8) * mm});
            skLineSegment(sketch, "E124.MirrorCS", {"start": v(2.5, -19.8) * mm, "end": v(0, -19.8) * mm});
            skLineSegment(sketch, "E125.MirrorCS", {"start": v(2.5, -16.3) * mm, "end": v(2.5, -19.8) * mm});
            skLineSegment(sketch, "E126.1.0", {"start": v(15.37, 5.99) * mm, "end": v(18.4, 7.74) * mm});
            skLineSegment(sketch, "E126.1.1", {"start": v(18.4, 7.74) * mm, "end": v(17.16, 9.9) * mm});
            skLineSegment(sketch, "E126.1.2", {"start": v(15.9, 12.07) * mm, "end": v(17.16, 9.9) * mm});
            skLineSegment(sketch, "E126.1.3", {"start": v(12.87, 10.32) * mm, "end": v(15.9, 12.07) * mm});
            skLineSegment(sketch, "E126.2.0", {"start": v(-12.87, 10.32) * mm, "end": v(-15.9, 12.07) * mm});
            skLineSegment(sketch, "E126.2.1", {"start": v(-15.9, 12.07) * mm, "end": v(-17.16, 9.9) * mm});
            skLineSegment(sketch, "E126.2.2", {"start": v(-18.4, 7.74) * mm, "end": v(-17.16, 9.9) * mm});
            skLineSegment(sketch, "E126.2.3", {"start": v(-15.37, 5.99) * mm, "end": v(-18.4, 7.74) * mm});
            skArc(sketch, "E127.trimOffspring", {"start": v(-15.37, 5.99) * mm, "mid": v(-14.29, -8.25) * mm, "end": v(-2.5, -16.3) * mm});
            skArc(sketch, "E128.trimOffspring", {"start": v(12.87, 10.32) * mm, "mid": v(0, 16.5) * mm, "end": v(-12.87, 10.32) * mm});
            skLineSegment(sketch, "E129", {"start": v(-34.02, 4) * mm, "end": v(-33, 4) * mm});
            skLineSegment(sketch, "E130.MirrorCS", {"start": v(-34.02, -4) * mm, "end": v(-33, -4) * mm});
            skLineSegment(sketch, "E131.MirrorCS", {"start": v(34.02, 4) * mm, "end": v(33, 4) * mm});
            skLineSegment(sketch, "E132.MirrorCS", {"start": v(34.02, -4) * mm, "end": v(33, -4) * mm});
            skArc(sketch, "E133", {"start": v(0, 20.5) * mm, "mid": v(-5.17, 19.84) * mm, "end": v(-10, 17.9) * mm});
            skArc(sketch, "E134", {"start": v(0, 29.25) * mm, "mid": v(-7.37, 28.3) * mm, "end": v(-14.27, 25.53) * mm});
            skArc(sketch, "E135", {"start": v(-14.27, 25.53) * mm, "mid": v(-15.95, 19.58) * mm, "end": v(-10, 17.9) * mm});
            skArc(sketch, "E136.MirrorCS", {"start": v(0, 20.5) * mm, "mid": v(5.17, 19.84) * mm, "end": v(10, 17.9) * mm});
            skArc(sketch, "E137.MirrorCS", {"start": v(14.27, 25.53) * mm, "mid": v(15.95, 19.58) * mm, "end": v(10, 17.9) * mm});
            skArc(sketch, "E138.MirrorCS", {"start": v(0, 29.25) * mm, "mid": v(7.37, 28.3) * mm, "end": v(14.27, 25.53) * mm});
            skArc(sketch, "E139.1.0", {"start": v(-17.75, -10.25) * mm, "mid": v(-19.76, -5.44) * mm, "end": v(-20.5, -0.29) * mm});
            skArc(sketch, "E139.1.1", {"start": v(-29.25, -0.41) * mm, "mid": v(-24.93, 4.03) * mm, "end": v(-20.5, -0.29) * mm});
            skArc(sketch, "E139.1.2", {"start": v(-25.33, -14.62) * mm, "mid": v(-28.2, -7.77) * mm, "end": v(-29.25, -0.41) * mm});
            skArc(sketch, "E139.1.3", {"start": v(-25.33, -14.62) * mm, "mid": v(-20.83, -20.54) * mm, "end": v(-14.98, -25.12) * mm});
            skArc(sketch, "E139.1.4", {"start": v(-14.98, -25.12) * mm, "mid": v(-8.98, -23.6) * mm, "end": v(-10.5, -17.6) * mm});
            skArc(sketch, "E139.1.5", {"start": v(-17.75, -10.25) * mm, "mid": v(-14.6, -14.4) * mm, "end": v(-10.5, -17.6) * mm});
            skArc(sketch, "E139.2.0", {"start": v(17.75, -10.25) * mm, "mid": v(14.6, -14.4) * mm, "end": v(10.5, -17.6) * mm});
            skArc(sketch, "E139.2.1", {"start": v(14.98, -25.12) * mm, "mid": v(8.98, -23.6) * mm, "end": v(10.5, -17.6) * mm});
            skArc(sketch, "E139.2.2", {"start": v(25.33, -14.63) * mm, "mid": v(20.83, -20.54) * mm, "end": v(14.98, -25.12) * mm});
            skArc(sketch, "E139.2.3", {"start": v(25.33, -14.63) * mm, "mid": v(28.2, -7.77) * mm, "end": v(29.25, -0.41) * mm});
            skArc(sketch, "E139.2.4", {"start": v(29.25, -0.41) * mm, "mid": v(24.93, 4.03) * mm, "end": v(20.5, -0.29) * mm});
            skArc(sketch, "E139.2.5", {"start": v(17.75, -10.25) * mm, "mid": v(19.76, -5.44) * mm, "end": v(20.5, -0.29) * mm});
            skSolve(sketch);
        }
        {
            var Q0;
            Q0=makeQuery(id+"F32.imprint","IMPRINT",FACE,{"disambiguationData":[TD([[makeQuery(id+"F32.imprint","IMPRINT",EDGE,{"derivedFrom":sQuery(id+"F32.wireOp",EDGE,"E120")}),-1.0]])]});
            var Q1;
            {var subQ0=sQuery(id+"F32.wireOp",EDGE,"E129");Q1=makeQuery(id+"F32.imprint","IMPRINT",FACE,{"disambiguationData":[TD([[makeQuery(id+"F32.imprint","IMPRINT",EDGE,{"derivedFrom":subQ0}),1.0]])]});}
            var Q2;
            {var subQ0=sQuery(id+"F32.wireOp",EDGE,"E129");Q2=makeQuery(id+"F32.imprint","IMPRINT",FACE,{"disambiguationData":[TD([[makeQuery(id+"F32.imprint","IMPRINT",EDGE,{"derivedFrom":subQ0}),-1.0]])]});}
            var Q3;
            {var subQ0=sQuery(id+"F32.wireOp",EDGE,"E130.MirrorCS");Q3=makeQuery(id+"F32.imprint","IMPRINT",FACE,{"disambiguationData":[TD([[makeQuery(id+"F32.imprint","IMPRINT",EDGE,{"derivedFrom":subQ0}),-1.0]])]});}
            var Q4;
            {var subQ0=sQuery(id+"F32.wireOp",EDGE,"E131.MirrorCS");Q4=makeQuery(id+"F32.imprint","IMPRINT",FACE,{"disambiguationData":[TD([[makeQuery(id+"F32.imprint","IMPRINT",EDGE,{"derivedFrom":subQ0}),1.0]])]});}
            extrude(context, id + "F33", {"entities" : qUnion([Q0, Q1, Q2, Q3, Q4]), "depth" : (getVariable(context, 'e')) * mm, "offsetDistance" : 25 * mm});
        }
        {
            var Q0;
            {var subQ0=sQuery(id+"F32.wireOp",EDGE,"E129");Q0=makeQuery(id+"F32.imprint","IMPRINT",FACE,{"disambiguationData":[TD([[makeQuery(id+"F32.imprint","IMPRINT",EDGE,{"derivedFrom":subQ0}),1.0]])]});}
            var Q1;
            {var subQ0=sQuery(id+"F32.wireOp",EDGE,"E130.MirrorCS");Q1=makeQuery(id+"F32.imprint","IMPRINT",FACE,{"disambiguationData":[TD([[makeQuery(id+"F32.imprint","IMPRINT",EDGE,{"derivedFrom":subQ0}),-1.0]])]});}
            extrude(context, id + "F34", {"entities" : qUnion([Q0, Q1]), "operationType" : NewBodyOperationType.ADD, "depth" : (2 * getVariable(context, 'e')) * mm, "offsetDistance" : 25 * mm});
        }
        {
            var Q0;
            Q0=makeQuery(id+"F33.opExtrude","SWEPT_FACE",FACE,{"disambiguationData":[OSD([sQuery(id+"F32.wireOp",EDGE,"E123"),sQuery(id+"F32.wireOp",EDGE,"E124.MirrorCS")])]});
            var sketch = newSketch(context, id + "F35", { "sketchPlane" : qUnion([Q0])});
            skLineSegment(sketch, "E140", {"start": v(30.51, 17.87) * mm, "end": v(21.51, 5.01) * mm, "construction": true});
            skLineSegment(sketch, "E141", {"start": v(-21.51, 5.01) * mm, "end": v(-30.51, 17.87) * mm, "construction": true});
            skLineSegment(sketch, "E142", {"start": v(-3.5, 39.75) * mm, "end": v(-2.25, 39.75) * mm});
            skLineSegment(sketch, "E143", {"start": v(-3.5, 39.75) * mm, "end": v(-3.5, 2.14) * mm});
            skLineSegment(sketch, "E144", {"start": v(-3.5, 2.14) * mm, "end": v(0, 2.14) * mm});
            skLineSegment(sketch, "E145", {"start": v(-2.25, 39.75) * mm, "end": v(-2.25, 41.75) * mm});
            skLineSegment(sketch, "E146", {"start": v(-2.25, 41.75) * mm, "end": v(-3.5, 41.75) * mm});
            skLineSegment(sketch, "E147", {"start": v(-3.5, 41.75) * mm, "end": v(-3.5, 42.75) * mm});
            skLineSegment(sketch, "E148", {"start": v(-3.5, 42.75) * mm, "end": v(0, 42.75) * mm});
            skLineSegment(sketch, "E149.MirrorCS", {"start": v(3.5, 42.75) * mm, "end": v(0, 42.75) * mm});
            skLineSegment(sketch, "E150.MirrorCS", {"start": v(3.5, 41.75) * mm, "end": v(3.5, 42.75) * mm});
            skLineSegment(sketch, "E151.MirrorCS", {"start": v(2.25, 41.75) * mm, "end": v(3.5, 41.75) * mm});
            skLineSegment(sketch, "E152.MirrorCS", {"start": v(2.25, 39.75) * mm, "end": v(2.25, 41.75) * mm});
            skLineSegment(sketch, "E153.MirrorCS", {"start": v(3.5, 39.75) * mm, "end": v(2.25, 39.75) * mm});
            skLineSegment(sketch, "E154.MirrorCS", {"start": v(3.5, 39.75) * mm, "end": v(3.5, 2.14) * mm});
            skLineSegment(sketch, "E155.MirrorCS", {"start": v(3.5, 2.14) * mm, "end": v(0, 2.14) * mm});
            skSolve(sketch);
        }
        {
            var Q0;
            Q0 = qSketchRegion(id + "F35", true);
            extrude(context, id + "F36", {"entities" : qUnion([Q0]), "depth" : 2.5 * mm, "offsetDistance" : 25 * mm});
        }
        {
            var Q0;
            Q0=qCreatedBy(makeId("Front.planeOp"),FACE);
            var sketch = newSketch(context, id + "F37", { "sketchPlane" : qUnion([Q0])});
            skArc(sketch, "E156", {"start": v(0, 4.14) * mm, "mid": v(-2.86, 5.88) * mm, "end": v(-2.64, 9.22) * mm});
            skLineSegment(sketch, "E157", {"start": v(-2.64, 9.22) * mm, "end": v(0, 13) * mm});
            skLineSegment(sketch, "E158.MirrorCS", {"start": v(2.64, 9.22) * mm, "end": v(0, 13) * mm});
            skArc(sketch, "E159.MirrorCS", {"start": v(0, 4.14) * mm, "mid": v(2.86, 5.88) * mm, "end": v(2.64, 9.22) * mm});
            skSolve(sketch);
        }
        {
            var Q0;
            Q0 = qSketchRegion(id + "F37", true);
            var Q1;
            Q1=makeQuery(id+"F11.opRevolve","SWEPT_FACE",FACE,{"disambiguationData":[OSD([sQuery(id+"F10.wireOp",EDGE,"E19")])]});
            extrude(context, id + "F38", {"entities" : qUnion([Q0]), "endBound" : BoundingType.UP_TO_SURFACE, "oppositeDirection" : true, "depth" : 25 * mm, "endBoundEntityFace" : qUnion([Q1]), "offsetDistance" : 25 * mm});
        }
        {
            var Q0;
            Q0=makeQuery(id+"F38.opExtrude","SWEPT_BODY",BODY,{"disambiguationData":[OSD([sQuery(id+"F37.wireOp",EDGE,"E156"),sQuery(id+"F37.wireOp",EDGE,"E157"),sQuery(id+"F37.wireOp",EDGE,"E158.MirrorCS"),sQuery(id+"F37.wireOp",EDGE,"E159.MirrorCS")])]});
            var Q1;
            Q1=sQuery(id+"F10.wireOp",EDGE,"E18");
            circularPattern(context, id + "F39", {"operationType" : NewBodyOperationType.REMOVE, "entities" : qUnion([Q0]), "axis" : qUnion([Q1]), "angle" : 360 * degree, "instanceCount" : 16, "equalSpace" : true});
        }
    });
